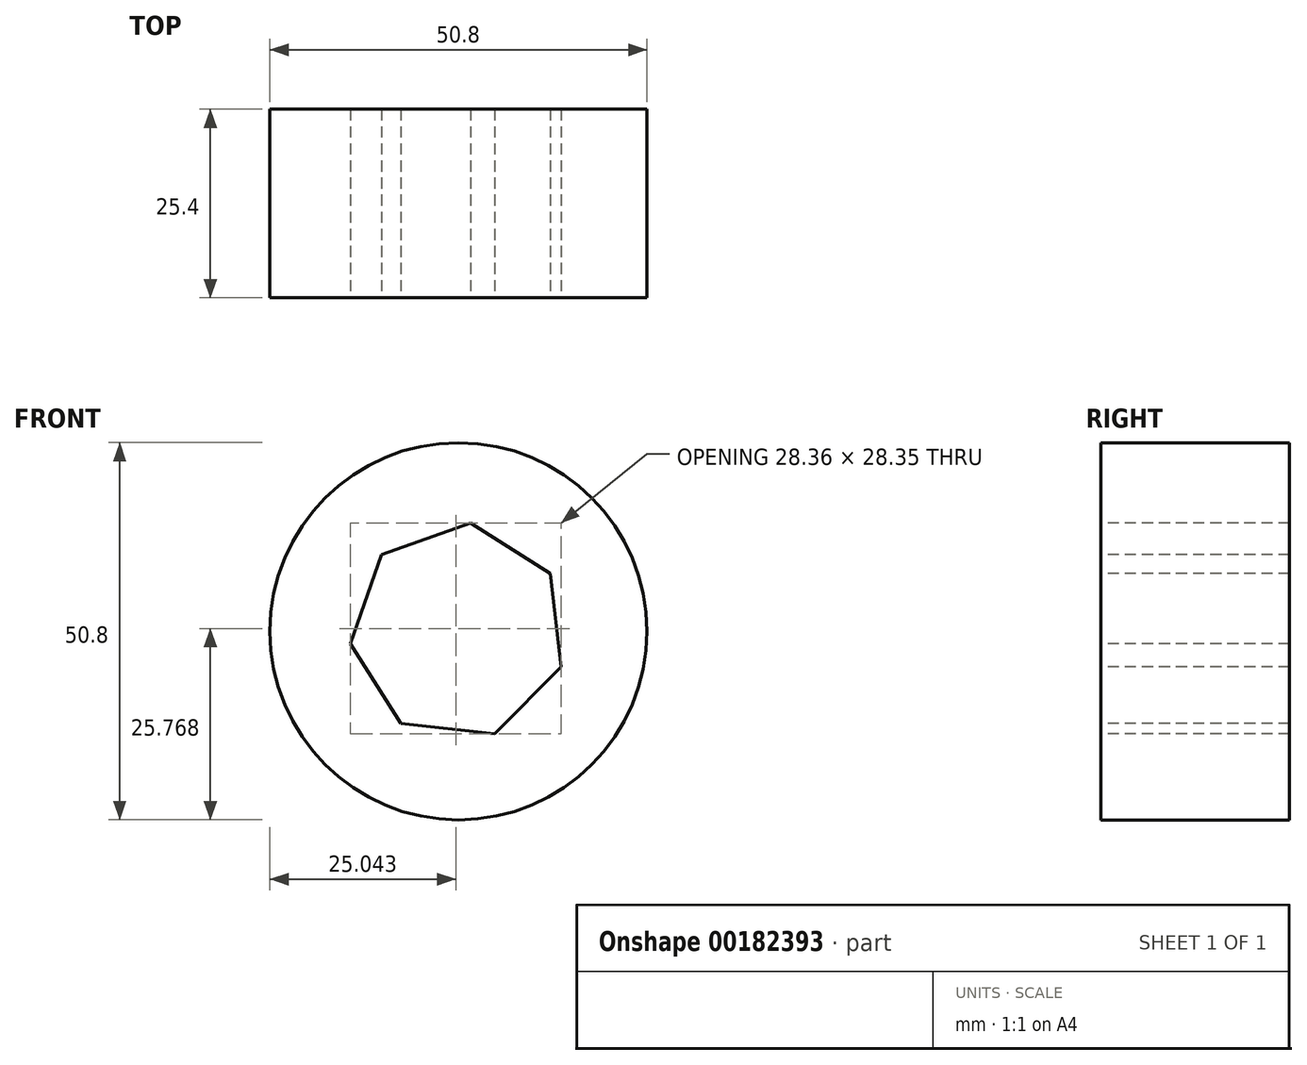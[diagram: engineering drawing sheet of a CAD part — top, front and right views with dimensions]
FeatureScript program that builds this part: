
annotation { "Feature Type Name" : "Feature", "Feature Type Description" : "" }
export const myFeature = defineFeature(function(context is Context, id is Id, definition is map)
    precondition{}
    {
        {
            var Q0;
            Q0=qCreatedBy(makeId("Front.planeOp"),FACE);
            var sketch = newSketch(context, id + "F0", { "sketchPlane" : qUnion([Q0])});
            skCircle(sketch, "E0", {"center": v(-42.66, 34.15) * mm, "radius": 25.4 * mm});
            skSolve(sketch);
        }
        {
            var Q0;
            Q0=makeQuery(id+"F0.imprint","IMPRINT",FACE,{"disambiguationData":[TD([[makeQuery(id+"F0.imprint","IMPRINT",EDGE,{"derivedFrom":sQuery(id+"F0.wireOp",EDGE,"E0")}),1.0]])]});
            extrude(context, id + "F1", {"entities" : qUnion([Q0]), "depth" : 25.4 * mm});
        }
        {
            var Q0;
            Q0=makeQuery(id+"F1.opExtrude","CAP_FACE",FACE,{"disambiguationData":[OSD([sQuery(id+"F0.wireOp",EDGE,"E0")])],"isStart":false});
            var sketch = newSketch(context, id + "F2", { "sketchPlane" : qUnion([Q0])});
            skCircle(sketch, "E1.cCircle", {"center": v(-42.66, 34.15) * mm, "radius": 13.19 * mm, "construction": true});
            skLineSegment(sketch, "E1.0", {"start": v(-57.2, 32.48) * mm, "end": v(-53.03, 44.48) * mm});
            skLineSegment(sketch, "E1.1", {"start": v(-53.03, 44.48) * mm, "end": v(-41.05, 48.7) * mm});
            skLineSegment(sketch, "E1.2", {"start": v(-41.05, 48.7) * mm, "end": v(-30.28, 41.96) * mm});
            skLineSegment(sketch, "E1.3", {"start": v(-30.28, 41.96) * mm, "end": v(-28.84, 29.34) * mm});
            skLineSegment(sketch, "E1.4", {"start": v(-28.84, 29.34) * mm, "end": v(-37.8, 20.34) * mm});
            skLineSegment(sketch, "E1.5", {"start": v(-37.8, 20.34) * mm, "end": v(-50.42, 21.74) * mm});
            skLineSegment(sketch, "E1.6", {"start": v(-50.42, 21.74) * mm, "end": v(-57.2, 32.48) * mm});
            skPoint(sketch, "E1.0.midPoint", {"position": v(-55.11, 38.48) * mm});
            skSolve(sketch);
        }
        {
            var Q0;
            Q0=makeQuery(id+"F2.imprint","IMPRINT",FACE,{"disambiguationData":[TD([[makeQuery(id+"F2.imprint","IMPRINT",EDGE,{"derivedFrom":sQuery(id+"F2.wireOp",EDGE,"E1.0")}),-1.0]])]});
            extrude(context, id + "F3", {"entities" : qUnion([Q0]), "operationType" : NewBodyOperationType.REMOVE, "oppositeDirection" : true, "depth" : 12.7 * mm});
        }
        {
            var Q0;
            Q0=makeQuery(id+"F3.boolean.opBoolean","COPY",FACE,{"derivedFrom":makeQuery(id+"F3.opExtrude","CAP_FACE",FACE,{"disambiguationData":[OSD([sQuery(id+"F2.wireOp",EDGE,"E1.0"),sQuery(id+"F2.wireOp",EDGE,"E1.1"),sQuery(id+"F2.wireOp",EDGE,"E1.2"),sQuery(id+"F2.wireOp",EDGE,"E1.3"),sQuery(id+"F2.wireOp",EDGE,"E1.4"),sQuery(id+"F2.wireOp",EDGE,"E1.5"),sQuery(id+"F2.wireOp",EDGE,"E1.6")])],"isStart":false})});
            extrude(context, id + "F4", {"entities" : qUnion([Q0]), "operationType" : NewBodyOperationType.REMOVE, "oppositeDirection" : true, "depth" : 50.8 * mm});
        }
    });
